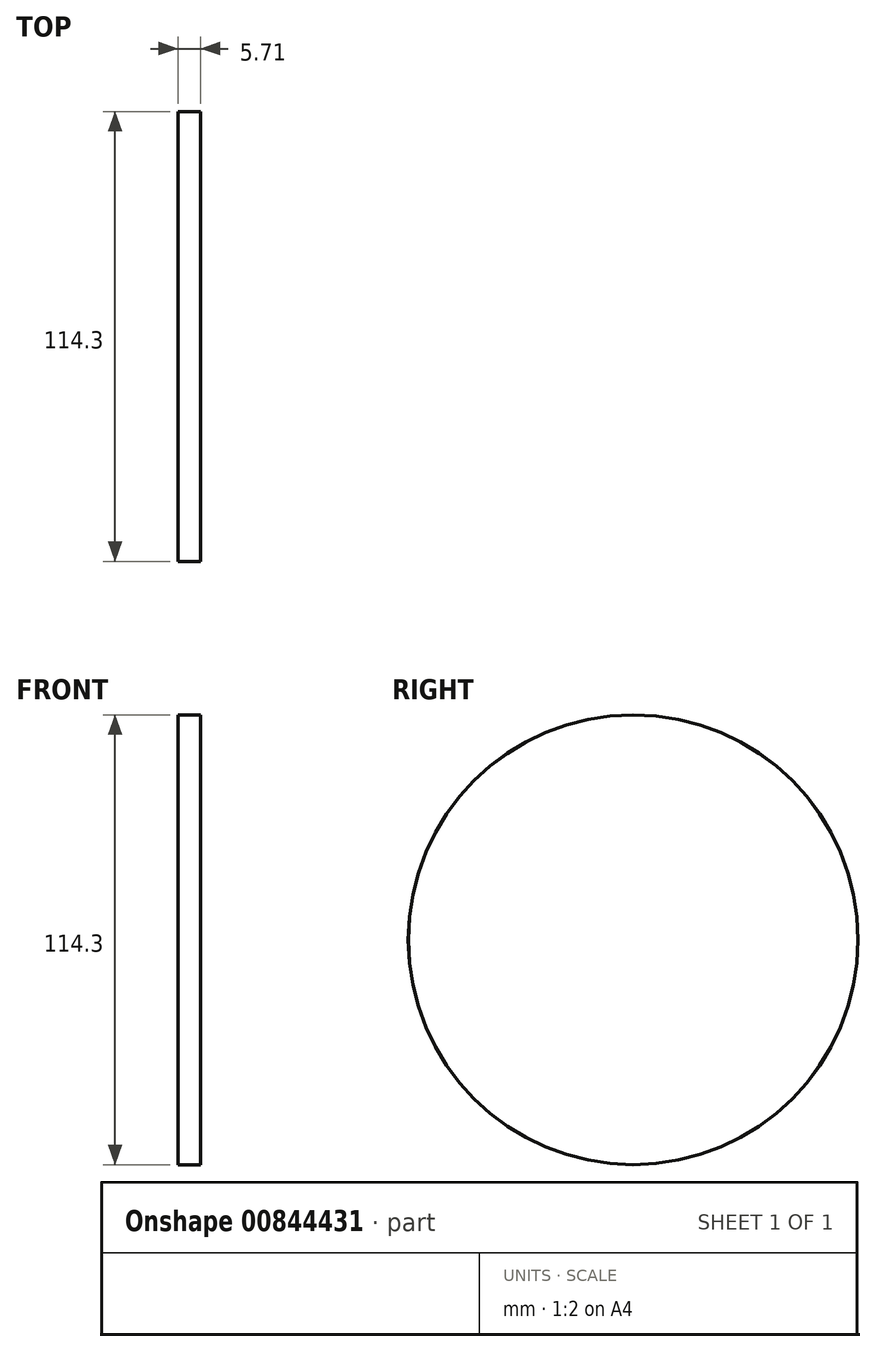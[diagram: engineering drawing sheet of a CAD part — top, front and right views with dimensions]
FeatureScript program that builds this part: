
annotation { "Feature Type Name" : "Feature", "Feature Type Description" : "" }
export const myFeature = defineFeature(function(context is Context, id is Id, definition is map)
    precondition{}
    {
        {
            var Q0;
            Q0=qCreatedBy(makeId("Right.planeOp"),FACE);
            var sketch = newSketch(context, id + "F0", { "sketchPlane" : qUnion([Q0])});
            skCircle(sketch, "E0", {"center": v(0, 0) * mm, "radius": 2.16 * mm});
            skCircle(sketch, "E1", {"center": v(0, 0) * mm, "radius": 57.15 * mm});
            skArc(sketch, "E2", {"start": v(-9.98, -1.9) * mm, "mid": v(-9.39, -3.89) * mm, "end": v(-8.4, -5.7) * mm});
            skArc(sketch, "E3", {"start": v(-1.9, 49.5) * mm, "mid": v(-18.95, 45.76) * mm, "end": v(-33.65, 36.34) * mm});
            skLineSegment(sketch, "E4", {"start": v(-1.9, 9.98) * mm, "end": v(-1.9, 49.5) * mm});
            skLineSegment(sketch, "E5", {"start": v(1.9, 9.98) * mm, "end": v(1.9, 49.5) * mm});
            skLineSegment(sketch, "E6.1.0", {"start": v(8.4, 5.7) * mm, "end": v(36.34, 33.65) * mm});
            skLineSegment(sketch, "E6.1.1", {"start": v(5.7, 8.4) * mm, "end": v(33.65, 36.34) * mm});
            skLineSegment(sketch, "E6.2.0", {"start": v(9.98, -1.9) * mm, "end": v(49.5, -1.9) * mm});
            skLineSegment(sketch, "E6.2.1", {"start": v(9.98, 1.9) * mm, "end": v(49.5, 1.9) * mm});
            skLineSegment(sketch, "E7.1.0", {"start": v(8.4, -5.7) * mm, "end": v(36.34, -33.65) * mm});
            skLineSegment(sketch, "E7.1.1", {"start": v(5.7, -8.4) * mm, "end": v(33.65, -36.34) * mm});
            skLineSegment(sketch, "E7.1.2", {"start": v(1.9, -9.98) * mm, "end": v(1.9, -49.5) * mm});
            skLineSegment(sketch, "E7.1.3", {"start": v(-1.9, -9.98) * mm, "end": v(-1.9, -49.5) * mm});
            skLineSegment(sketch, "E7.2.0", {"start": v(-5.7, -8.4) * mm, "end": v(-33.65, -36.34) * mm});
            skLineSegment(sketch, "E7.2.1", {"start": v(-8.4, -5.7) * mm, "end": v(-36.34, -33.65) * mm});
            skLineSegment(sketch, "E7.2.2", {"start": v(-9.98, -1.9) * mm, "end": v(-49.5, -1.9) * mm});
            skLineSegment(sketch, "E7.2.3", {"start": v(-9.98, 1.9) * mm, "end": v(-49.5, 1.9) * mm});
            skLineSegment(sketch, "E8.1.0", {"start": v(-5.7, 8.4) * mm, "end": v(-33.65, 36.34) * mm});
            skLineSegment(sketch, "E8.1.1", {"start": v(-8.4, 5.7) * mm, "end": v(-36.34, 33.65) * mm});
            skArc(sketch, "E9.trimOffspring", {"start": v(33.65, 36.34) * mm, "mid": v(18.95, 45.76) * mm, "end": v(1.9, 49.5) * mm});
            skArc(sketch, "E10.trimOffspring", {"start": v(49.5, 1.9) * mm, "mid": v(45.76, 18.95) * mm, "end": v(36.34, 33.65) * mm});
            skArc(sketch, "E11.trimOffspring", {"start": v(36.34, -33.65) * mm, "mid": v(45.76, -18.95) * mm, "end": v(49.5, -1.9) * mm});
            skArc(sketch, "E12.trimOffspring", {"start": v(1.9, -49.5) * mm, "mid": v(18.95, -45.76) * mm, "end": v(33.65, -36.34) * mm});
            skArc(sketch, "E13.trimOffspring", {"start": v(-33.65, -36.34) * mm, "mid": v(-18.95, -45.76) * mm, "end": v(-1.9, -49.5) * mm});
            skArc(sketch, "E14.trimOffspring", {"start": v(-49.5, -1.9) * mm, "mid": v(-45.76, -18.95) * mm, "end": v(-36.34, -33.65) * mm});
            skArc(sketch, "E15.trimOffspring", {"start": v(-36.34, 33.65) * mm, "mid": v(-45.76, 18.95) * mm, "end": v(-49.5, 1.9) * mm});
            skArc(sketch, "E16.trimOffspring", {"start": v(-8.4, 5.7) * mm, "mid": v(-9.39, 3.89) * mm, "end": v(-9.98, 1.9) * mm});
            skArc(sketch, "E17.trimOffspring", {"start": v(-1.9, 9.98) * mm, "mid": v(-3.89, 9.39) * mm, "end": v(-5.7, 8.4) * mm});
            skArc(sketch, "E18.trimOffspring", {"start": v(5.7, 8.4) * mm, "mid": v(3.89, 9.39) * mm, "end": v(1.9, 9.98) * mm});
            skArc(sketch, "E19.trimOffspring", {"start": v(9.98, 1.9) * mm, "mid": v(9.39, 3.89) * mm, "end": v(8.4, 5.7) * mm});
            skArc(sketch, "E20.trimOffspring", {"start": v(8.4, -5.7) * mm, "mid": v(9.39, -3.89) * mm, "end": v(9.98, -1.9) * mm});
            skArc(sketch, "E21.trimOffspring", {"start": v(1.9, -9.98) * mm, "mid": v(3.89, -9.39) * mm, "end": v(5.7, -8.4) * mm});
            skArc(sketch, "E22.trimOffspring", {"start": v(-5.7, -8.4) * mm, "mid": v(-3.89, -9.39) * mm, "end": v(-1.9, -9.98) * mm});
            skSolve(sketch);
        }
        {
            var Q0;
            Q0=qSketchRegion(id+"F0",true);
            extrude(context, id + "F1", {"entities" : qUnion([Q0]), "depth" : 3.8 * mm, "offsetDistance" : 25.4 * mm});
        }
        {
            var Q0;
            Q0=qCreatedBy(makeId("Front.planeOp"),FACE);
            var sketch = newSketch(context, id + "F2", { "sketchPlane" : qUnion([Q0])});
            skArc(sketch, "E23", {"start": v(3.81, 57.14) * mm, "mid": v(1.9, 55.27) * mm, "end": v(0, 57.14) * mm});
            skLineSegment(sketch, "E24", {"start": v(-7.97, 0) * mm, "end": v(9.15, 0) * mm, "construction": true});
            skLineSegment(sketch, "E25", {"start": v(3.81, 57.14) * mm, "end": v(0, 57.14) * mm});
            skSolve(sketch);
        }
        {
            var Q0;
            Q0=qSketchRegion(id+"F2",true);
            var Q1;
            Q1=sQuery(id+"F2.wireOp",EDGE,"E24");
            revolve(context, id + "F3", {"operationType" : NewBodyOperationType.REMOVE, "surfaceOperationType" : NewSurfaceOperationType.NEW, "entities" : qUnion([Q0]), "axis" : qUnion([Q1]), "revolveType" : RevolveType.FULL});
        }
        {
            var Q0;
            Q0=qCreatedBy(makeId("Right.planeOp"),FACE);
            var sketch = newSketch(context, id + "F4", { "sketchPlane" : qUnion([Q0])});
            skCircle(sketch, "E26", {"center": v(0, 0) * mm, "radius": 6.1 * mm, "construction": true});
            skLineSegment(sketch, "E27.0", {"start": v(-3.52, 6.1) * mm, "end": v(3.52, 6.1) * mm});
            skLineSegment(sketch, "E27.1", {"start": v(3.52, 6.1) * mm, "end": v(7.04, 0) * mm});
            skLineSegment(sketch, "E27.2", {"start": v(7.04, 0) * mm, "end": v(3.52, -6.1) * mm});
            skLineSegment(sketch, "E27.3", {"start": v(3.52, -6.1) * mm, "end": v(-3.52, -6.1) * mm});
            skLineSegment(sketch, "E27.4", {"start": v(-3.52, -6.1) * mm, "end": v(-7.04, 0) * mm});
            skLineSegment(sketch, "E27.5", {"start": v(-7.04, 0) * mm, "end": v(-3.52, 6.1) * mm});
            skPoint(sketch, "E27.0.midPoint", {"position": v(0, 6.1) * mm});
            skCircle(sketch, "E28", {"center": v(0, 0) * mm, "radius": 10.16 * mm});
            skSolve(sketch);
        }
        {
            var Q0;
            Q0=qSketchRegion(id+"F4",true);
            extrude(context, id + "F5", {"entities" : qUnion([Q0]), "operationType" : NewBodyOperationType.ADD, "oppositeDirection" : true, "depth" : 7.62 * mm, "offsetDistance" : 25.4 * mm});
        }
        {
            var Q0;
            Q0=qCreatedBy(makeId("Right.planeOp"),FACE);
            var sketch = newSketch(context, id + "F6", { "sketchPlane" : qUnion([Q0])});
            skPoint(sketch, "E29.center", {"position": v(0, 0) * mm});
            skCircle(sketch, "E30", {"center": v(0, 0) * mm, "radius": 57.15 * mm});
            skArc(sketch, "E31", {"start": v(-1.9, 49.5) * mm, "mid": v(-18.95, 45.76) * mm, "end": v(-33.65, 36.34) * mm});
            skLineSegment(sketch, "E32", {"start": v(-1.9, 9.98) * mm, "end": v(-1.9, 49.5) * mm});
            skLineSegment(sketch, "E33", {"start": v(1.9, 9.98) * mm, "end": v(1.9, 49.5) * mm});
            skLineSegment(sketch, "E34.1.0", {"start": v(8.4, 5.7) * mm, "end": v(36.34, 33.65) * mm});
            skLineSegment(sketch, "E34.1.1", {"start": v(5.7, 8.4) * mm, "end": v(33.65, 36.34) * mm});
            skLineSegment(sketch, "E34.2.0", {"start": v(9.98, -1.9) * mm, "end": v(49.5, -1.9) * mm});
            skLineSegment(sketch, "E34.2.1", {"start": v(9.98, 1.9) * mm, "end": v(49.5, 1.9) * mm});
            skLineSegment(sketch, "E35.1.0", {"start": v(8.4, -5.7) * mm, "end": v(36.34, -33.65) * mm});
            skLineSegment(sketch, "E35.1.1", {"start": v(5.7, -8.4) * mm, "end": v(33.65, -36.34) * mm});
            skLineSegment(sketch, "E35.1.2", {"start": v(1.9, -9.98) * mm, "end": v(1.9, -49.5) * mm});
            skLineSegment(sketch, "E35.1.3", {"start": v(-1.9, -9.98) * mm, "end": v(-1.9, -49.5) * mm});
            skLineSegment(sketch, "E35.2.0", {"start": v(-5.7, -8.4) * mm, "end": v(-33.65, -36.34) * mm});
            skLineSegment(sketch, "E35.2.1", {"start": v(-8.4, -5.7) * mm, "end": v(-36.34, -33.65) * mm});
            skLineSegment(sketch, "E35.2.2", {"start": v(-9.98, -1.9) * mm, "end": v(-49.5, -1.9) * mm});
            skLineSegment(sketch, "E35.2.3", {"start": v(-9.98, 1.9) * mm, "end": v(-49.5, 1.9) * mm});
            skLineSegment(sketch, "E36.1.0", {"start": v(-5.7, 8.4) * mm, "end": v(-33.65, 36.34) * mm});
            skLineSegment(sketch, "E36.1.1", {"start": v(-8.4, 5.7) * mm, "end": v(-36.34, 33.65) * mm});
            skArc(sketch, "E37.trimOffspring", {"start": v(33.65, 36.34) * mm, "mid": v(18.95, 45.76) * mm, "end": v(1.9, 49.5) * mm});
            skArc(sketch, "E38.trimOffspring", {"start": v(49.5, 1.9) * mm, "mid": v(45.76, 18.95) * mm, "end": v(36.34, 33.65) * mm});
            skArc(sketch, "E39.trimOffspring", {"start": v(36.34, -33.65) * mm, "mid": v(45.76, -18.95) * mm, "end": v(49.5, -1.9) * mm});
            skArc(sketch, "E40.trimOffspring", {"start": v(1.9, -49.5) * mm, "mid": v(18.95, -45.76) * mm, "end": v(33.65, -36.34) * mm});
            skArc(sketch, "E41.trimOffspring", {"start": v(-33.65, -36.34) * mm, "mid": v(-18.95, -45.76) * mm, "end": v(-1.9, -49.5) * mm});
            skArc(sketch, "E42.trimOffspring", {"start": v(-49.5, -1.9) * mm, "mid": v(-45.76, -18.95) * mm, "end": v(-36.34, -33.65) * mm});
            skArc(sketch, "E43.trimOffspring", {"start": v(-36.34, 33.65) * mm, "mid": v(-45.76, 18.95) * mm, "end": v(-49.5, 1.9) * mm});
            skArc(sketch, "E44", {"start": v(-8.4, 5.7) * mm, "mid": v(-9.39, 3.89) * mm, "end": v(-9.98, 1.9) * mm});
            skArc(sketch, "E45.trimOffspring", {"start": v(-9.98, -1.9) * mm, "mid": v(-9.39, -3.89) * mm, "end": v(-8.4, -5.7) * mm});
            skArc(sketch, "E46.trimOffspring", {"start": v(-5.7, -8.4) * mm, "mid": v(-3.89, -9.39) * mm, "end": v(-1.9, -9.98) * mm});
            skArc(sketch, "E47.trimOffspring", {"start": v(1.9, -9.98) * mm, "mid": v(3.89, -9.39) * mm, "end": v(5.7, -8.4) * mm});
            skArc(sketch, "E48.trimOffspring", {"start": v(8.4, -5.7) * mm, "mid": v(9.39, -3.89) * mm, "end": v(9.98, -1.9) * mm});
            skArc(sketch, "E49.trimOffspring", {"start": v(9.98, 1.9) * mm, "mid": v(9.39, 3.89) * mm, "end": v(8.4, 5.7) * mm});
            skArc(sketch, "E50.trimOffspring", {"start": v(5.7, 8.4) * mm, "mid": v(3.89, 9.39) * mm, "end": v(1.9, 9.98) * mm});
            skArc(sketch, "E51.trimOffspring", {"start": v(-1.9, 9.98) * mm, "mid": v(-3.89, 9.39) * mm, "end": v(-5.7, 8.4) * mm});
            skCircle(sketch, "E52", {"center": v(0, 0) * mm, "radius": 7.62 * mm});
            skSolve(sketch);
        }
        {
            var Q0;
            Q0 = qSketchRegion(id + "F6", true);
            extrude(context, id + "F7", {"entities" : qUnion([Q0]), "operationType" : NewBodyOperationType.ADD, "depth" : -3.8 * mm, "offsetDistance" : 25.4 * mm});
        }
        {
            var Q0;
            Q0=qCreatedBy(makeId("Front.planeOp"),FACE);
            var sketch = newSketch(context, id + "F8", { "sketchPlane" : qUnion([Q0])});
            skArc(sketch, "E53", {"start": v(0, 57.14) * mm, "mid": v(-1.91, 55.24) * mm, "end": v(-3.81, 57.16) * mm});
            skLineSegment(sketch, "E54", {"start": v(-3.81, 57.16) * mm, "end": v(0, 57.14) * mm});
            skLineSegment(sketch, "E55", {"start": v(12.06, 0) * mm, "end": v(-19.51, 0) * mm, "construction": true});
            skSolve(sketch);
        }
        {
            var Q0;
            Q0 = qSketchRegion(id + "F8", true);
            var Q1;
            Q1=sQuery(id+"F8.wireOp",EDGE,"E55");
            revolve(context, id + "F9", {"operationType" : NewBodyOperationType.REMOVE, "surfaceOperationType" : NewSurfaceOperationType.NEW, "entities" : qUnion([Q0]), "axis" : qUnion([Q1]), "revolveType" : RevolveType.FULL, "oppositeDirection" : true});
        }
        {
            var Q0;
            Q0=qCreatedBy(makeId("Right.planeOp"),FACE);
            cPlane(context, id + "F10", {"entities" : qUnion([Q0]), "cplaneType" : CPlaneType.OFFSET, "offset" : 3.8 * mm, "oppositeDirection" : true, "width" : 152.4 * mm, "height" : 152.4 * mm});
        }
        {
            var Q0;
            Q0=qCreatedBy(id+"F10.planeOp",FACE);
            var sketch = newSketch(context, id + "F11", { "sketchPlane" : qUnion([Q0])});
            skPoint(sketch, "E56.center", {"position": v(0, 0) * mm});
            skCircle(sketch, "E57", {"center": v(0, 0) * mm, "radius": 57.15 * mm});
            skArc(sketch, "E58", {"start": v(-1.9, 49.5) * mm, "mid": v(-18.95, 45.76) * mm, "end": v(-33.65, 36.34) * mm});
            skLineSegment(sketch, "E59", {"start": v(-1.9, 9.98) * mm, "end": v(-1.9, 49.5) * mm});
            skLineSegment(sketch, "E60", {"start": v(1.9, 9.98) * mm, "end": v(1.9, 49.5) * mm});
            skLineSegment(sketch, "E61.1.0", {"start": v(8.4, 5.7) * mm, "end": v(36.34, 33.65) * mm});
            skLineSegment(sketch, "E61.1.1", {"start": v(5.7, 8.4) * mm, "end": v(33.65, 36.34) * mm});
            skLineSegment(sketch, "E61.2.0", {"start": v(9.98, -1.9) * mm, "end": v(49.5, -1.9) * mm});
            skLineSegment(sketch, "E61.2.1", {"start": v(9.98, 1.9) * mm, "end": v(49.5, 1.9) * mm});
            skLineSegment(sketch, "E62.1.0", {"start": v(8.4, -5.7) * mm, "end": v(36.34, -33.65) * mm});
            skLineSegment(sketch, "E62.1.1", {"start": v(5.7, -8.4) * mm, "end": v(33.65, -36.34) * mm});
            skLineSegment(sketch, "E62.1.2", {"start": v(1.9, -9.98) * mm, "end": v(1.9, -49.5) * mm});
            skLineSegment(sketch, "E62.1.3", {"start": v(-1.9, -9.98) * mm, "end": v(-1.9, -49.5) * mm});
            skLineSegment(sketch, "E62.2.0", {"start": v(-5.7, -8.4) * mm, "end": v(-33.65, -36.34) * mm});
            skLineSegment(sketch, "E62.2.1", {"start": v(-8.4, -5.7) * mm, "end": v(-36.34, -33.65) * mm});
            skLineSegment(sketch, "E62.2.2", {"start": v(-9.98, -1.9) * mm, "end": v(-49.5, -1.9) * mm});
            skLineSegment(sketch, "E62.2.3", {"start": v(-9.98, 1.9) * mm, "end": v(-49.5, 1.9) * mm});
            skLineSegment(sketch, "E63.1.0", {"start": v(-5.7, 8.4) * mm, "end": v(-33.65, 36.34) * mm});
            skLineSegment(sketch, "E63.1.1", {"start": v(-8.4, 5.7) * mm, "end": v(-36.34, 33.65) * mm});
            skArc(sketch, "E64.trimOffspring", {"start": v(33.65, 36.34) * mm, "mid": v(18.95, 45.76) * mm, "end": v(1.9, 49.5) * mm});
            skArc(sketch, "E65.trimOffspring", {"start": v(49.5, 1.9) * mm, "mid": v(45.76, 18.95) * mm, "end": v(36.34, 33.65) * mm});
            skArc(sketch, "E66.trimOffspring", {"start": v(36.34, -33.65) * mm, "mid": v(45.76, -18.95) * mm, "end": v(49.5, -1.9) * mm});
            skArc(sketch, "E67.trimOffspring", {"start": v(1.9, -49.5) * mm, "mid": v(18.95, -45.76) * mm, "end": v(33.65, -36.34) * mm});
            skArc(sketch, "E68.trimOffspring", {"start": v(-33.65, -36.34) * mm, "mid": v(-18.95, -45.76) * mm, "end": v(-1.9, -49.5) * mm});
            skArc(sketch, "E69.trimOffspring", {"start": v(-49.5, -1.9) * mm, "mid": v(-45.76, -18.95) * mm, "end": v(-36.34, -33.65) * mm});
            skArc(sketch, "E70.trimOffspring", {"start": v(-36.34, 33.65) * mm, "mid": v(-45.76, 18.95) * mm, "end": v(-49.5, 1.9) * mm});
            skArc(sketch, "E71", {"start": v(-8.4, 5.7) * mm, "mid": v(-9.39, 3.89) * mm, "end": v(-9.98, 1.9) * mm});
            skArc(sketch, "E72.trimOffspring", {"start": v(-9.98, -1.9) * mm, "mid": v(-9.39, -3.89) * mm, "end": v(-8.4, -5.7) * mm});
            skArc(sketch, "E73.trimOffspring", {"start": v(-5.7, -8.4) * mm, "mid": v(-3.89, -9.39) * mm, "end": v(-1.9, -9.98) * mm});
            skArc(sketch, "E74.trimOffspring", {"start": v(1.9, -9.98) * mm, "mid": v(3.89, -9.39) * mm, "end": v(5.7, -8.4) * mm});
            skArc(sketch, "E75.trimOffspring", {"start": v(8.4, -5.7) * mm, "mid": v(9.39, -3.89) * mm, "end": v(9.98, -1.9) * mm});
            skArc(sketch, "E76.trimOffspring", {"start": v(9.98, 1.9) * mm, "mid": v(9.39, 3.89) * mm, "end": v(8.4, 5.7) * mm});
            skArc(sketch, "E77.trimOffspring", {"start": v(5.7, 8.4) * mm, "mid": v(3.89, 9.39) * mm, "end": v(1.9, 9.98) * mm});
            skArc(sketch, "E78.trimOffspring", {"start": v(-1.9, 9.98) * mm, "mid": v(-3.89, 9.39) * mm, "end": v(-5.7, 8.4) * mm});
            skCircle(sketch, "E79", {"center": v(0, 0) * mm, "radius": 7.62 * mm});
            skSolve(sketch);
        }
        {
            var Q0;
            Q0 = qSketchRegion(id + "F11", true);
            extrude(context, id + "F12", {"entities" : qUnion([Q0]), "operationType" : NewBodyOperationType.ADD, "depth" : -3.8 * mm, "offsetDistance" : 25.4 * mm});
        }
        {
            var Q0;
            Q0=qCreatedBy(makeId("Front.planeOp"),FACE);
            var sketch = newSketch(context, id + "F13", { "sketchPlane" : qUnion([Q0])});
            skLineSegment(sketch, "E80", {"start": v(-19.97, 0) * mm, "end": v(12.16, 0) * mm, "construction": true});
            skArc(sketch, "E81", {"start": v(-3.81, 57.15) * mm, "mid": v(-5.71, 55.24) * mm, "end": v(-7.62, 57.14) * mm});
            skLineSegment(sketch, "E82", {"start": v(-5.71, 57.14) * mm, "end": v(-5.71, 55.97) * mm, "construction": true});
            skLineSegment(sketch, "E83", {"start": v(-7.62, 57.14) * mm, "end": v(-3.81, 57.15) * mm});
            skSolve(sketch);
        }
        {
            var Q0;
            Q0 = qSketchRegion(id + "F13", true);
            var Q1;
            Q1=sQuery(id+"F13.wireOp",EDGE,"E80");
            revolve(context, id + "F14", {"operationType" : NewBodyOperationType.REMOVE, "surfaceOperationType" : NewSurfaceOperationType.NEW, "entities" : qUnion([Q0]), "axis" : qUnion([Q1]), "revolveType" : RevolveType.FULL, "oppositeDirection" : true});
        }
        {
            var Q0;
            Q0=makeQuery(id+"F14.boolean.opBoolean","SPLIT",BODY,{"disambiguationData":[OD(1.0)],"derivedFrom":makeQuery(id+"F1.opExtrude","SWEPT_BODY",BODY,{"disambiguationData":[OSD([sQuery(id+"F0.wireOp",EDGE,"E0"),sQuery(id+"F0.wireOp",EDGE,"E1"),sQuery(id+"F0.wireOp",EDGE,"E2"),sQuery(id+"F0.wireOp",EDGE,"E3"),sQuery(id+"F0.wireOp",EDGE,"E4"),sQuery(id+"F0.wireOp",EDGE,"E5"),sQuery(id+"F0.wireOp",EDGE,"E6.1.0"),sQuery(id+"F0.wireOp",EDGE,"E6.1.1"),sQuery(id+"F0.wireOp",EDGE,"E6.2.0"),sQuery(id+"F0.wireOp",EDGE,"E6.2.1"),sQuery(id+"F0.wireOp",EDGE,"E7.1.0"),sQuery(id+"F0.wireOp",EDGE,"E7.1.1"),sQuery(id+"F0.wireOp",EDGE,"E7.1.2"),sQuery(id+"F0.wireOp",EDGE,"E7.1.3"),sQuery(id+"F0.wireOp",EDGE,"E7.2.0"),sQuery(id+"F0.wireOp",EDGE,"E7.2.1"),sQuery(id+"F0.wireOp",EDGE,"E7.2.2"),sQuery(id+"F0.wireOp",EDGE,"E7.2.3"),sQuery(id+"F0.wireOp",EDGE,"E8.1.0"),sQuery(id+"F0.wireOp",EDGE,"E8.1.1"),sQuery(id+"F0.wireOp",EDGE,"E9.trimOffspring"),sQuery(id+"F0.wireOp",EDGE,"E10.trimOffspring"),sQuery(id+"F0.wireOp",EDGE,"E11.trimOffspring"),sQuery(id+"F0.wireOp",EDGE,"E12.trimOffspring"),sQuery(id+"F0.wireOp",EDGE,"E13.trimOffspring"),sQuery(id+"F0.wireOp",EDGE,"E14.trimOffspring"),sQuery(id+"F0.wireOp",EDGE,"E15.trimOffspring"),sQuery(id+"F0.wireOp",EDGE,"E16.trimOffspring"),sQuery(id+"F0.wireOp",EDGE,"E17.trimOffspring"),sQuery(id+"F0.wireOp",EDGE,"E18.trimOffspring"),sQuery(id+"F0.wireOp",EDGE,"E19.trimOffspring"),sQuery(id+"F0.wireOp",EDGE,"E20.trimOffspring"),sQuery(id+"F0.wireOp",EDGE,"E21.trimOffspring"),sQuery(id+"F0.wireOp",EDGE,"E22.trimOffspring")])]})});
            deleteBodies(context, id + "F15", {"entities" : qUnion([Q0])});
        }
    });
